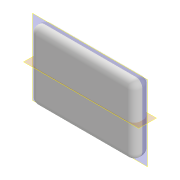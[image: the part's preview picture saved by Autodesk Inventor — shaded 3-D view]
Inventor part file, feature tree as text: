
AUTODESK INVENTOR PART (.ipt)
format: ipt  version: 2022 (Build 260153000, 153)  size: 109,056 bytes
history: native  units: in
note: dims shown in document units (in); Inventor stores cm internally (conversion verified against a paired STEP export)
features: plane x2, extrude x1, fillet x1, sketch x1
ambient origin geometry x8: Origin, YZ Plane, XZ Plane, XY Plane, X Axis, Y Axis, Z Axis, Center Point
bodies: Solid1 (feature_tree)
feature tree (5):
  extrude  "Extrusion1"  Depth=2.4016in
  fillet  "Fillet1"  Radius=0.5669in
  plane  "Work Plane1"
  plane  "Work Plane2"
  sketch  "Sketch1"  dims[d0=3.6614in d1=2.4016in d2=0.5669in d3=0.0in d4=0.2362in]
